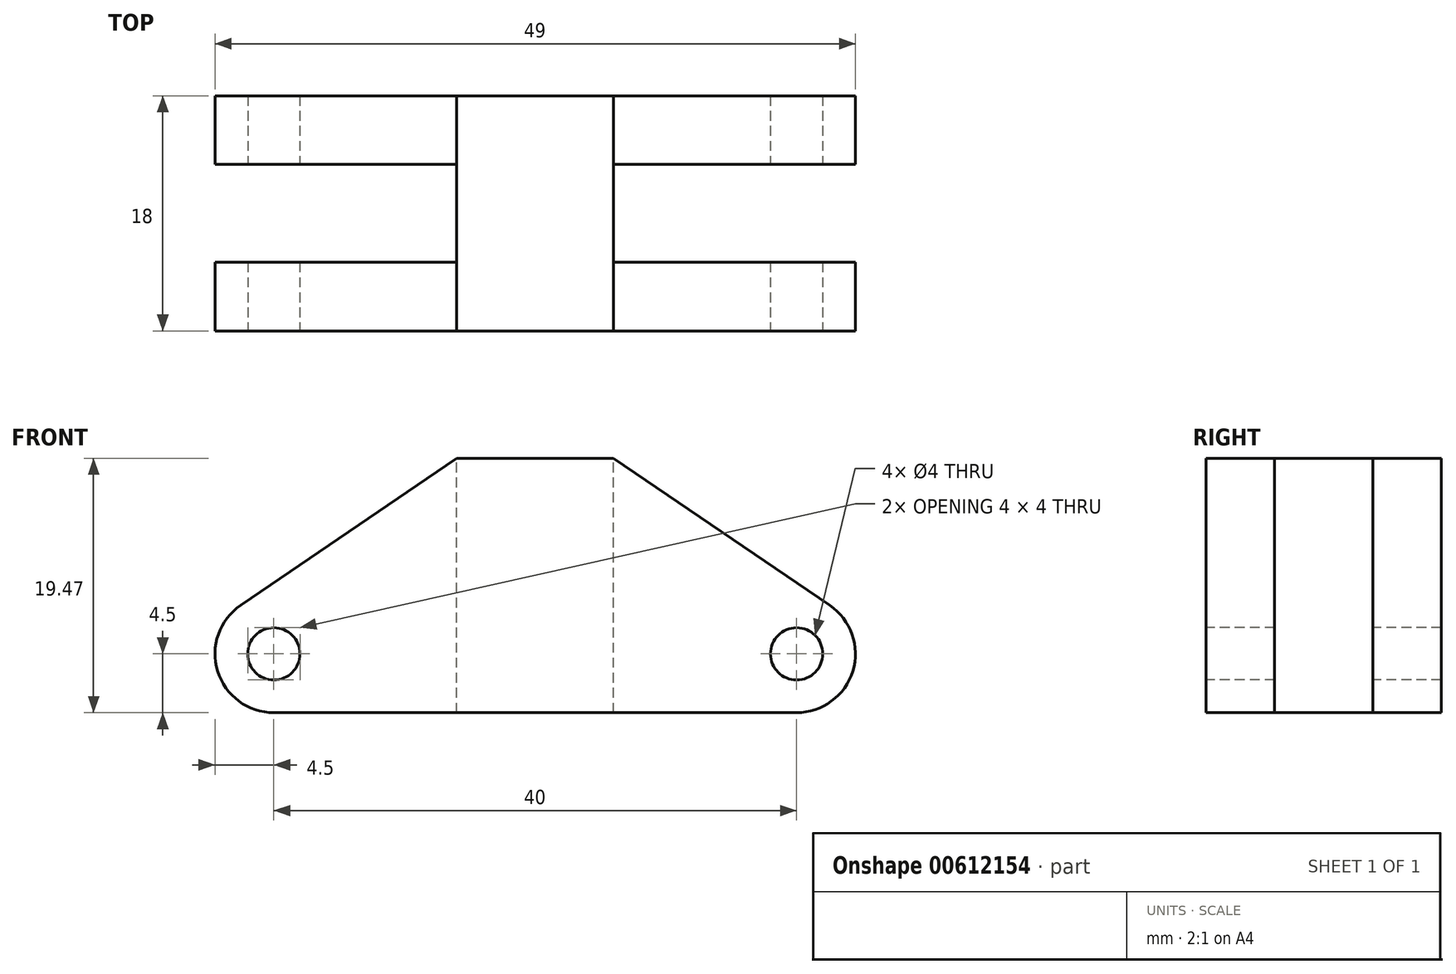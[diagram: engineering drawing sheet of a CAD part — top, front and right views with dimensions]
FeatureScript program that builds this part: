
annotation { "Feature Type Name" : "Feature", "Feature Type Description" : "" }
export const myFeature = defineFeature(function(context is Context, id is Id, definition is map)
    precondition{}
    {
        {
            var Q0;
            Q0=qCreatedBy(makeId("Front.planeOp"),FACE);
            var sketch = newSketch(context, id + "F0", { "sketchPlane" : qUnion([Q0])});
            skLineSegment(sketch, "E0", {"start": v(0, 0) * mm, "end": v(-20, 0) * mm});
            skLineSegment(sketch, "E1", {"start": v(0, 0) * mm, "end": v(20, 0) * mm});
            skArc(sketch, "E2", {"start": v(-20, 0) * mm, "mid": v(-24.3, 3.18) * mm, "end": v(-22.53, 8.22) * mm});
            skArc(sketch, "E3", {"start": v(20, 0) * mm, "mid": v(24.3, 3.18) * mm, "end": v(22.53, 8.22) * mm});
            skLineSegment(sketch, "E4", {"start": v(-22.53, 8.22) * mm, "end": v(-6, 19.47) * mm});
            skLineSegment(sketch, "E5", {"start": v(22.53, 8.22) * mm, "end": v(6, 19.47) * mm});
            skLineSegment(sketch, "E6", {"start": v(-6, 19.47) * mm, "end": v(6, 19.47) * mm});
            skSolve(sketch);
        }
        {
            var Q0;
            Q0=makeQuery(id+"F0.imprint","IMPRINT",FACE,{"disambiguationData":[TD([[makeQuery(id+"F0.imprint","IMPRINT",EDGE,{"derivedFrom":sQuery(id+"F0.wireOp",EDGE,"E0")}),-1.0]])]});
            extrude(context, id + "F1", {"entities" : qUnion([Q0]), "depth" : 18 * mm, "offsetDistance" : 25 * mm});
        }
        {
            var Q0;
            Q0=makeQuery(id+"F1.opExtrude","SWEPT_FACE",FACE,{"disambiguationData":[OSD([sQuery(id+"F0.wireOp",EDGE,"E6")])]});
            var sketch = newSketch(context, id + "F2", { "sketchPlane" : qUnion([Q0])});
            skLineSegment(sketch, "E7", {"start": v(0, 0) * mm, "end": v(0, -18) * mm, "construction": true});
            skLineSegment(sketch, "E8", {"start": v(6, -9) * mm, "end": v(-6, -9) * mm, "construction": true});
            skLineSegment(sketch, "E9.bottom", {"start": v(31.92, -12.75) * mm, "end": v(-31.92, -12.75) * mm});
            skLineSegment(sketch, "E9.top", {"start": v(31.92, -5.25) * mm, "end": v(-31.92, -5.25) * mm});
            skLineSegment(sketch, "E9.left", {"start": v(31.92, -12.75) * mm, "end": v(31.92, -5.25) * mm});
            skLineSegment(sketch, "E9.right", {"start": v(-31.92, -12.75) * mm, "end": v(-31.92, -5.25) * mm});
            skPoint(sketch, "E9.middle", {"position": v(0, -9) * mm});
            skSolve(sketch);
        }
        {
            var Q0;
            {var subQ0=sQuery(id+"F2.wireOp",EDGE,"E9.right");Q0=makeQuery(id+"F2.imprint","IMPRINT",FACE,{"disambiguationData":[TD([[makeQuery(id+"F2.imprint","IMPRINT",EDGE,{"derivedFrom":subQ0}),-1.0]])]});}
            var Q1;
            {var subQ0=sQuery(id+"F2.wireOp",EDGE,"E9.left");Q1=makeQuery(id+"F2.imprint","IMPRINT",FACE,{"disambiguationData":[TD([[makeQuery(id+"F2.imprint","IMPRINT",EDGE,{"derivedFrom":subQ0}),1.0]])]});}
            extrude(context, id + "F3", {"entities" : qUnion([Q0, Q1]), "operationType" : NewBodyOperationType.REMOVE, "oppositeDirection" : true, "depth" : 25 * mm, "offsetDistance" : 25 * mm});
        }
        {
            var Q0;
            Q0=makeQuery(id+"F1.opExtrude","CAP_FACE",FACE,{"disambiguationData":[OSD([sQuery(id+"F0.wireOp",EDGE,"E0"),sQuery(id+"F0.wireOp",EDGE,"E1"),sQuery(id+"F0.wireOp",EDGE,"E2"),sQuery(id+"F0.wireOp",EDGE,"E3"),sQuery(id+"F0.wireOp",EDGE,"E4"),sQuery(id+"F0.wireOp",EDGE,"E5"),sQuery(id+"F0.wireOp",EDGE,"E6")])],"isStart":false});
            var sketch = newSketch(context, id + "F4", { "sketchPlane" : qUnion([Q0])});
            skCircle(sketch, "E10", {"center": v(-20, 4.5) * mm, "radius": 2 * mm});
            skCircle(sketch, "E11", {"center": v(20, 4.5) * mm, "radius": 2 * mm});
            skSolve(sketch);
        }
        {
            var Q0;
            Q0=makeQuery(id+"F4.imprint","IMPRINT",FACE,{"disambiguationData":[TD([[makeQuery(id+"F4.imprint","IMPRINT",EDGE,{"derivedFrom":sQuery(id+"F4.wireOp",EDGE,"E10")}),1.0]])]});
            var Q1;
            Q1=makeQuery(id+"F4.imprint","IMPRINT",FACE,{"disambiguationData":[TD([[makeQuery(id+"F4.imprint","IMPRINT",EDGE,{"derivedFrom":sQuery(id+"F4.wireOp",EDGE,"E11")}),1.0]])]});
            extrude(context, id + "F5", {"entities" : qUnion([Q0, Q1]), "operationType" : NewBodyOperationType.REMOVE, "oppositeDirection" : true, "depth" : 25 * mm, "offsetDistance" : 25 * mm});
        }
    });
